# Revit family: NBS_Allermuir_OffcChrs_Obris_2SeatSofa
name_source: partatom
category: Furniture
revit_build: Autodesk Revit 2018 (Build: 20190510_1515(x64)
units: mm (PartAtom-declared; Revit-internal decimal feet)

## family parameters
Always vertical = Yes
Cut with Voids When Loaded = No
Room Calculation Point = No
Shared = No
Work Plane-Based = No

## types (1)
- Obris_2SeatSofa_OBR02
    ArmHeight = 770 mm
    AssetType = Movable
    BIMObjectName = NBS_Allermuir_DomesticChairs_Obris_OBR02
    Category = Pr_40_50_12_81:Sofas
    Description = Two seat sofa
    DurationUnit = year
    ExpectedLife = 10
    Features = Tubular Steel back frame with foam overmould and tensioned fabric, Tradtional carcass seat with dual density seat foam, Foam core with feather and down back and arm cushions, Solid Beech feet with a Black colour wash finish, Reversable plastic/felt glides
    FeetMaterial = NBS_Allermuir_Beech_Black
    Finish = Fabric
    IfcExportAs = IfcFurnitureType
    IfcExportType = SOFA
    IsBuiltIn = No
    ManufacturerName = Allermuir
    ManufacturerURL = www.allermuir.co.uk
    Material = Fabric, Nylon 6, PU foam, Plywood, Aluminium Casting, Aluminium Extrusion, Steel
    ModelNumber = OBR02
    ModelReference = Obris
    NBSCertification = www.nationalbimlibrary.com/cert/sfpj1txk
    NBSDescription = Domestic Chairs
    NBSReference = 45-35-20/365
    Name = DomesticChairs_OBR02_Obris_Allermuir
    NominalDepth = 900 mm
    NominalHeight = 770 mm
    NominalLength = 0 mm  [stored 0 ft]
    NominalWidth = 1900 mm
    ProductInformation = https://www.allermuir.com
    SeatDepth = 800 mm
    SeatHeight = 415 mm
    SeatMaterial = NBS_Allermuir_Fabric
    SeatWidth = 1690 mm
    Size = 900 x 770 x 1900 mm
    Status = UNSET
    Style = Sofa
    SustainabilityPerformance = 99% recyclable
    Uniclass2015Code = Pr_40_50_12_81
    Uniclass2015Title = Sofas
    Uniclass2015Version = Products v1.15
    Version = 1
    WarrantyDescription = Allermuir warrant that its manufactured products are free from manufacturing defects - in materials or workmanship - for a period of five (5) years. , Allermuir will repair, or replace (at Allermuir's sole discretion) with comparable free of charge materials / components, any product / component which fails under normal use in a single shift environment, as a result of a defect in the materials and/ or workmanship
    WarrantyDurationParts = 5
    WarrantyDurationUnit = year

note: [stored X ft] marks values corroborated as IEEE doubles in the binary element streams (Revit-internal decimal feet)

## geometry (parser evidence)
native form markers: Extrusion x3, Sweep x2
no freeform markers — native parametric forms only
